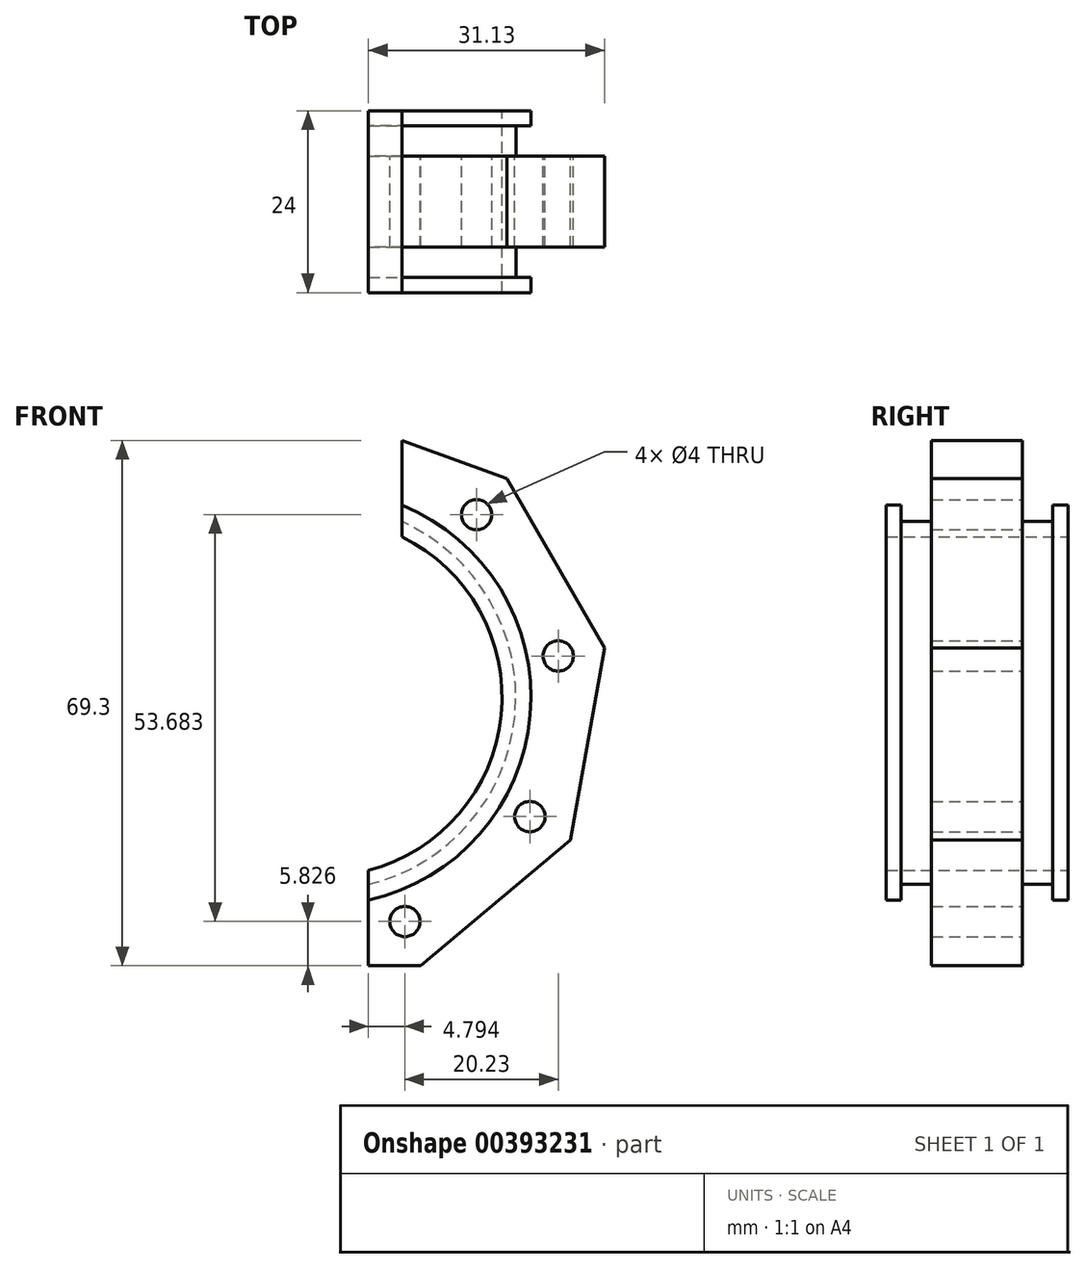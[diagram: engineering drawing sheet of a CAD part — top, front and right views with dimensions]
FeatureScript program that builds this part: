
annotation { "Feature Type Name" : "Feature", "Feature Type Description" : "" }
export const myFeature = defineFeature(function(context is Context, id is Id, definition is map)
    precondition{}
    {
        {
            var Q0;
            Q0=qCreatedBy(makeId("Front.planeOp"),FACE);
            var sketch = newSketch(context, id + "F0", { "sketchPlane" : qUnion([Q0])});
            skLineSegment(sketch, "E0.5", {"start": v(10.36, 33.9) * mm, "end": v(24.22, 28.86) * mm});
            skLineSegment(sketch, "E0.6", {"start": v(24.22, 28.86) * mm, "end": v(37.1, 6.54) * mm});
            skLineSegment(sketch, "E0.7", {"start": v(37.1, 6.54) * mm, "end": v(32.62, -18.84) * mm});
            skLineSegment(sketch, "E0.8", {"start": v(32.62, -18.84) * mm, "end": v(12.88, -35.4) * mm});
            skLineSegment(sketch, "E1", {"start": v(5.97, -26.74) * mm, "end": v(5.97, -24.69) * mm});
            skLineSegment(sketch, "E2", {"start": v(10.36, 25.36) * mm, "end": v(10.36, 23.19) * mm});
            skCircle(sketch, "E3", {"center": v(20.23, 24.1) * mm, "radius": 2 * mm});
            skCircle(sketch, "E4", {"center": v(31, 5.47) * mm, "radius": 2 * mm});
            skCircle(sketch, "E5", {"center": v(27.26, -15.74) * mm, "radius": 2 * mm});
            skLineSegment(sketch, "E6", {"start": v(10.36, 25.36) * mm, "end": v(10.36, 33.9) * mm});
            skLineSegment(sketch, "E7", {"start": v(5.97, -26.74) * mm, "end": v(5.97, -35.4) * mm});
            skArc(sketch, "E8", {"start": v(5.97, -24.69) * mm, "mid": v(25.3, -2.32) * mm, "end": v(10.36, 23.19) * mm});
            skLineSegment(sketch, "E9", {"start": v(5.97, -24.69) * mm, "end": v(5.97, -22.69) * mm});
            skLineSegment(sketch, "E10", {"start": v(10.36, 23.19) * mm, "end": v(10.36, 21.19) * mm});
            skArc(sketch, "E11", {"start": v(10.36, 21.19) * mm, "mid": v(23.47, -2.34) * mm, "end": v(5.97, -22.82) * mm});
            skLineSegment(sketch, "E12", {"start": v(12.88, -35.4) * mm, "end": v(5.97, -35.4) * mm});
            skArc(sketch, "E13", {"start": v(5.97, -26.74) * mm, "mid": v(27.3, -2.3) * mm, "end": v(10.36, 25.36) * mm});
            skCircle(sketch, "E14", {"center": v(10.76, -29.57) * mm, "radius": 2 * mm});
            skSolve(sketch);
        }
        {
            var Q0;
            Q0=makeQuery(id+"F0.imprint","IMPRINT",FACE,{"disambiguationData":[TD([[makeQuery(id+"F0.imprint","IMPRINT",EDGE,{"derivedFrom":sQuery(id+"F0.wireOp",EDGE,"E0.5")}),-1.0]])]});
            var Q1;
            Q1=makeQuery(id+"F0.imprint","IMPRINT",FACE,{"disambiguationData":[TD([[makeQuery(id+"F0.imprint","IMPRINT",EDGE,{"derivedFrom":sQuery(id+"F0.wireOp",EDGE,"E1")}),-1.0]])]});
            extrude(context, id + "F1", {"entities" : qUnion([Q0, Q1]), "endBound" : BoundingType.SYMMETRIC, "depth" : 12 * mm});
        }
        {
            var Q0;
            {var subQ0=sQuery(id+"F0.wireOp",EDGE,"E8");Q0=makeQuery(id+"F0.imprint","IMPRINT",FACE,{"disambiguationData":[TD([[makeQuery(id+"F0.imprint","IMPRINT",EDGE,{"derivedFrom":subQ0}),1.0]])]});}
            extrude(context, id + "F2", {"entities" : qUnion([Q0]), "operationType" : NewBodyOperationType.ADD, "endBound" : BoundingType.SYMMETRIC, "depth" : 24 * mm});
        }
        {
            var Q0;
            Q0=makeQuery(id+"F2.opExtrude","CAP_FACE",FACE,{"disambiguationData":[OSD([sQuery(id+"F0.wireOp",EDGE,"E8"),sQuery(id+"F0.wireOp",EDGE,"E9"),sQuery(id+"F0.wireOp",EDGE,"E10"),sQuery(id+"F0.wireOp",EDGE,"E11")])],"isStart":false});
            var sketch = newSketch(context, id + "F3", { "sketchPlane" : qUnion([Q0])});
            skArc(sketch, "E15.0", {"start": v(5.97, -26.74) * mm, "mid": v(27.3, -2.3) * mm, "end": v(10.36, 25.36) * mm});
            skLineSegment(sketch, "E16.0", {"start": v(10.36, 25.36) * mm, "end": v(10.36, 23.19) * mm});
            skArc(sketch, "E17.0", {"start": v(5.97, -24.69) * mm, "mid": v(25.3, -2.32) * mm, "end": v(10.36, 23.19) * mm});
            skLineSegment(sketch, "E18.0", {"start": v(5.97, -26.74) * mm, "end": v(5.97, -24.69) * mm});
            skSolve(sketch);
        }
        {
            var Q0;
            Q0 = qSketchRegion(id + "F3", true);
            extrude(context, id + "F4", {"entities" : qUnion([Q0]), "operationType" : NewBodyOperationType.ADD, "oppositeDirection" : true, "depth" : 2 * mm});
        }
        {
            var Q0;
            Q0=makeQuery(id+"F2.opExtrude","CAP_FACE",FACE,{"disambiguationData":[OSD([sQuery(id+"F0.wireOp",EDGE,"E8"),sQuery(id+"F0.wireOp",EDGE,"E9"),sQuery(id+"F0.wireOp",EDGE,"E10"),sQuery(id+"F0.wireOp",EDGE,"E11")])],"isStart":true});
            var sketch = newSketch(context, id + "F5", { "sketchPlane" : qUnion([Q0])});
            skArc(sketch, "E19.0", {"start": v(-5.97, -26.74) * mm, "mid": v(-27.3, -2.3) * mm, "end": v(-10.36, 25.36) * mm});
            skLineSegment(sketch, "E20.0", {"start": v(-10.36, 25.36) * mm, "end": v(-10.36, 23.19) * mm});
            skArc(sketch, "E21.0", {"start": v(-5.97, -24.69) * mm, "mid": v(-25.3, -2.32) * mm, "end": v(-10.36, 23.19) * mm});
            skLineSegment(sketch, "E22.0", {"start": v(-5.97, -26.74) * mm, "end": v(-5.97, -24.69) * mm});
            skSolve(sketch);
        }
        {
            var Q0;
            Q0 = qSketchRegion(id + "F5", true);
            extrude(context, id + "F6", {"entities" : qUnion([Q0]), "operationType" : NewBodyOperationType.ADD, "oppositeDirection" : true, "depth" : 2 * mm});
        }
    });
